# Revit family: 306_3a99b926ff1f4e68be58d4fb30fde6
name_source: partatom
category: Pipe Accessories
units: mm (PartAtom-declared; Revit-internal decimal feet)

## family parameters
Always vertical = Yes
Cut with Voids When Loaded = No
Part Type = Valve - Breaks Into
Round Connector Dimension = Use Diameter
Shared = No
Work Plane-Based = No

## types (14) — shared parameters
CAT0 = Yes
Description = 3-way rotary mixing valve VRG132, PN10 external thread
L2D_Min = 3048 mm
MC = No
Manufacturer = ESBE
QmdConnectorList = 301;D;302;D
URL = http://www.esbe.eu
magiPartTypeId = 306
magiProductFamilyId = 3a99b926ff1f4e68be58d4fb30fde6

## per-type parameters (varying)
| type | A1 | AR | B | C | D | D1 | L2D | W2D | X1 | X2 | Y0 | Y00 | Y2 | Y3 | Y6 | Y7 | Y9 | Z5 | Z5__ve | magiProductId |
| VRG132 15-0.4 G 3/4 | 27 mm | 27 mm | 72 mm | 32 mm  [stored 0.104987 ft] | 15 mm | 50 mm  [stored 0.164042 ft] | 52 mm  [stored 0.170604 ft] | 15 mm  [stored 0.0492126 ft] | 36 mm  [stored 0.11811 ft] | 26 mm  [stored 0.0853018 ft] | 8 mm  [stored 0.0262467 ft] | 8 mm  [stored 0.0262467 ft] | 8 mm  [stored 0.0262467 ft] | 18 mm  [stored 0.0590551 ft] | 17 mm  [stored 0.0557743 ft] | 15 mm  [stored 0.0492126 ft] | 14 mm  [stored 0.0459318 ft] | 9 mm  [stored 0.0295276 ft] | -9 mm  [stored -0.0295276 ft] | 42bb4f0f5b9f45f8ac982adfdfa688 |
| VRG132 50-40 G 2¼ | 46 mm  [stored 0.150919 ft] | 46 mm  [stored 0.150919 ft] | 140 mm | 46 mm  [stored 0.150919 ft] | 50 mm | 64 mm | 120 mm | 50 mm  [stored 0.164042 ft] | 70 mm | 60 mm | 26 mm  [stored 0.0853018 ft] | 25 mm  [stored 0.082021 ft] | 26 mm  [stored 0.0853018 ft] | 44 mm  [stored 0.144357 ft] | 43 mm | 41 mm  [stored 0.134514 ft] | 40 mm  [stored 0.131234 ft] | 14 mm  [stored 0.0459318 ft] | -14 mm | 9705669eed7b457eaaa12ba5fa8e1b |
| VRG132 40-25 G 2 | 40 mm  [stored 0.131234 ft] | 40 mm  [stored 0.131234 ft] | 126 mm | 44 mm  [stored 0.144357 ft] | 40 mm | 60 mm | 106 mm | 40 mm  [stored 0.131234 ft] | 63 mm | 53 mm  [stored 0.173885 ft] | 20 mm  [stored 0.0656168 ft] | 20 mm  [stored 0.0656168 ft] | 21 mm | 38 mm | 37 mm  [stored 0.121391 ft] | 36 mm  [stored 0.11811 ft] | 35 mm  [stored 0.114829 ft] | 13 mm  [stored 0.0426509 ft] | -13 mm  [stored -0.0426509 ft] | 7704420eb76542f9966813aaeb78f1 |
| VRG132 32-16 G 1 1/2 | 36 mm  [stored 0.11811 ft] | 36 mm  [stored 0.11811 ft] | 114 mm | 37 mm  [stored 0.121391 ft] | 32 mm | 55 mm | 94 mm | 32 mm  [stored 0.104987 ft] | 57 mm | 47 mm  [stored 0.154199 ft] | 16 mm  [stored 0.0524934 ft] | 16 mm  [stored 0.0524934 ft] | 17 mm  [stored 0.0557743 ft] | 34 mm  [stored 0.111549 ft] | 33 mm | 31 mm  [stored 0.101706 ft] | 30 mm  [stored 0.0984252 ft] | 11 mm | -11 mm | 0fe858b763dd45928668f1722e74c2 |
| VRG132 25-6.3 G 1 1/4 | 31 mm  [stored 0.101706 ft] | 31 mm  [stored 0.101706 ft] | 92 mm | 34 mm  [stored 0.111549 ft] | 25 mm | 52 mm  [stored 0.170604 ft] | 62 mm | 25 mm  [stored 0.082021 ft] | 46 mm  [stored 0.150919 ft] | 31 mm  [stored 0.101706 ft] | 13 mm  [stored 0.0426509 ft] | 13 mm  [stored 0.0426509 ft] | 13 mm  [stored 0.0426509 ft] | 22 mm | 21 mm | 19 mm | 18 mm  [stored 0.0590551 ft] | 10 mm  [stored 0.0328084 ft] | -10 mm  [stored -0.0328084 ft] | 4c830626f7584bb48dd0ce417f718d |
| VRG132 25-10 G 1 1/4 | 31 mm  [stored 0.101706 ft] | 31 mm  [stored 0.101706 ft] | 82 mm | 34 mm  [stored 0.111549 ft] | 25 mm | 52 mm  [stored 0.170604 ft] | 62 mm | 25 mm  [stored 0.082021 ft] | 41 mm  [stored 0.134514 ft] | 31 mm  [stored 0.101706 ft] | 13 mm  [stored 0.0426509 ft] | 13 mm  [stored 0.0426509 ft] | 13 mm  [stored 0.0426509 ft] | 22 mm | 21 mm | 19 mm | 18 mm  [stored 0.0590551 ft] | 10 mm  [stored 0.0328084 ft] | -10 mm  [stored -0.0328084 ft] | b2f078a88a6d49fcb45a9839bba755 |
| VRG132 20-6.3 G 1 | 27 mm | 27 mm | 72 mm | 32 mm  [stored 0.104987 ft] | 20 mm | 50 mm  [stored 0.164042 ft] | 52 mm  [stored 0.170604 ft] | 20 mm  [stored 0.0656168 ft] | 36 mm  [stored 0.11811 ft] | 26 mm  [stored 0.0853018 ft] | 10 mm  [stored 0.0328084 ft] | 10 mm  [stored 0.0328084 ft] | 11 mm | 18 mm  [stored 0.0590551 ft] | 17 mm  [stored 0.0557743 ft] | 15 mm  [stored 0.0492126 ft] | 14 mm  [stored 0.0459318 ft] | 9 mm  [stored 0.0295276 ft] | -9 mm  [stored -0.0295276 ft] | 62cb3c4cadab4e8a800e5bf97d49f7 |
| VRG132 20-4 G 1 | 27 mm | 27 mm | 72 mm | 32 mm  [stored 0.104987 ft] | 20 mm | 50 mm  [stored 0.164042 ft] | 52 mm  [stored 0.170604 ft] | 20 mm  [stored 0.0656168 ft] | 36 mm  [stored 0.11811 ft] | 26 mm  [stored 0.0853018 ft] | 10 mm  [stored 0.0328084 ft] | 10 mm  [stored 0.0328084 ft] | 11 mm | 18 mm  [stored 0.0590551 ft] | 17 mm  [stored 0.0557743 ft] | 15 mm  [stored 0.0492126 ft] | 14 mm  [stored 0.0459318 ft] | 9 mm  [stored 0.0295276 ft] | -9 mm  [stored -0.0295276 ft] | 206ba77146ed4f3cbc179b0ada63c3 |
| VRG132 20-2.5 G 1 | 27 mm | 27 mm | 72 mm | 32 mm  [stored 0.104987 ft] | 20 mm | 50 mm  [stored 0.164042 ft] | 52 mm  [stored 0.170604 ft] | 20 mm  [stored 0.0656168 ft] | 36 mm  [stored 0.11811 ft] | 26 mm  [stored 0.0853018 ft] | 10 mm  [stored 0.0328084 ft] | 10 mm  [stored 0.0328084 ft] | 11 mm | 18 mm  [stored 0.0590551 ft] | 17 mm  [stored 0.0557743 ft] | 15 mm  [stored 0.0492126 ft] | 14 mm  [stored 0.0459318 ft] | 9 mm  [stored 0.0295276 ft] | -9 mm  [stored -0.0295276 ft] | f80c9f0935ec411d9f60d48614f355 |
| VRG132 15-4 G 3/4 | 27 mm | 27 mm | 72 mm | 32 mm  [stored 0.104987 ft] | 15 mm | 50 mm  [stored 0.164042 ft] | 52 mm  [stored 0.170604 ft] | 15 mm  [stored 0.0492126 ft] | 36 mm  [stored 0.11811 ft] | 26 mm  [stored 0.0853018 ft] | 8 mm  [stored 0.0262467 ft] | 8 mm  [stored 0.0262467 ft] | 8 mm  [stored 0.0262467 ft] | 18 mm  [stored 0.0590551 ft] | 17 mm  [stored 0.0557743 ft] | 15 mm  [stored 0.0492126 ft] | 14 mm  [stored 0.0459318 ft] | 9 mm  [stored 0.0295276 ft] | -9 mm  [stored -0.0295276 ft] | fe7f65cdded94510a3b29f9c41a709 |
| VRG132 15-2.5 G 3/4 | 27 mm | 27 mm | 72 mm | 32 mm  [stored 0.104987 ft] | 15 mm | 50 mm  [stored 0.164042 ft] | 52 mm  [stored 0.170604 ft] | 15 mm  [stored 0.0492126 ft] | 36 mm  [stored 0.11811 ft] | 26 mm  [stored 0.0853018 ft] | 8 mm  [stored 0.0262467 ft] | 8 mm  [stored 0.0262467 ft] | 8 mm  [stored 0.0262467 ft] | 18 mm  [stored 0.0590551 ft] | 17 mm  [stored 0.0557743 ft] | 15 mm  [stored 0.0492126 ft] | 14 mm  [stored 0.0459318 ft] | 9 mm  [stored 0.0295276 ft] | -9 mm  [stored -0.0295276 ft] | 3f8961bd99a441daa262fcd3a11a57 |
| VRG132 15-1.6 G 3/4 | 27 mm | 27 mm | 72 mm | 32 mm  [stored 0.104987 ft] | 15 mm | 50 mm  [stored 0.164042 ft] | 52 mm  [stored 0.170604 ft] | 15 mm  [stored 0.0492126 ft] | 36 mm  [stored 0.11811 ft] | 26 mm  [stored 0.0853018 ft] | 8 mm  [stored 0.0262467 ft] | 8 mm  [stored 0.0262467 ft] | 8 mm  [stored 0.0262467 ft] | 18 mm  [stored 0.0590551 ft] | 17 mm  [stored 0.0557743 ft] | 15 mm  [stored 0.0492126 ft] | 14 mm  [stored 0.0459318 ft] | 9 mm  [stored 0.0295276 ft] | -9 mm  [stored -0.0295276 ft] | 16b904cc4563401e94d6078217eef2 |
| VRG132 15-1.0 G 3/4 | 27 mm | 27 mm | 72 mm | 32 mm  [stored 0.104987 ft] | 15 mm | 50 mm  [stored 0.164042 ft] | 52 mm  [stored 0.170604 ft] | 15 mm  [stored 0.0492126 ft] | 36 mm  [stored 0.11811 ft] | 26 mm  [stored 0.0853018 ft] | 8 mm  [stored 0.0262467 ft] | 8 mm  [stored 0.0262467 ft] | 8 mm  [stored 0.0262467 ft] | 18 mm  [stored 0.0590551 ft] | 17 mm  [stored 0.0557743 ft] | 15 mm  [stored 0.0492126 ft] | 14 mm  [stored 0.0459318 ft] | 9 mm  [stored 0.0295276 ft] | -9 mm  [stored -0.0295276 ft] | e1852ca2e4db4559a0753b4eadb138 |
| VRG132 15-0.63 G 3/4 | 27 mm | 27 mm | 72 mm | 32 mm  [stored 0.104987 ft] | 15 mm | 50 mm  [stored 0.164042 ft] | 52 mm  [stored 0.170604 ft] | 15 mm  [stored 0.0492126 ft] | 36 mm  [stored 0.11811 ft] | 26 mm  [stored 0.0853018 ft] | 8 mm  [stored 0.0262467 ft] | 8 mm  [stored 0.0262467 ft] | 8 mm  [stored 0.0262467 ft] | 18 mm  [stored 0.0590551 ft] | 17 mm  [stored 0.0557743 ft] | 15 mm  [stored 0.0492126 ft] | 14 mm  [stored 0.0459318 ft] | 9 mm  [stored 0.0295276 ft] | -9 mm  [stored -0.0295276 ft] | 286f79b829f64cc49c50e000a798f9 |

note: column(s) folded — value = type name in every type: magiProductCode

note: [stored X ft] marks values corroborated as IEEE doubles in the binary element streams (Revit-internal decimal feet)

## geometry (parser evidence)
native form markers: Sweep x1
no freeform markers — native parametric forms only
